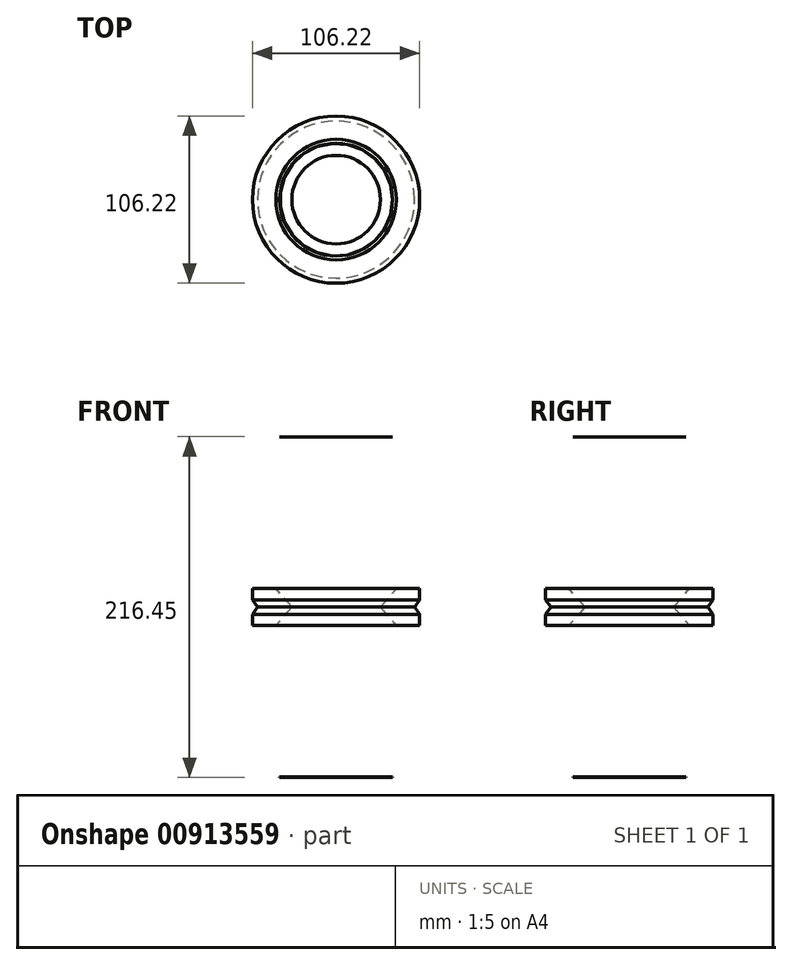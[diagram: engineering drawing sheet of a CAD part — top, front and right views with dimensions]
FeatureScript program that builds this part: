
annotation { "Feature Type Name" : "Feature", "Feature Type Description" : "" }
export const myFeature = defineFeature(function(context is Context, id is Id, definition is map)
    precondition{}
    {
        {
            var Q0;
            Q0=qCreatedBy(makeId("Front.planeOp"),FACE);
            var sketch = newSketch(context, id + "F0", { "sketchPlane" : qUnion([Q0])});
            skLineSegment(sketch, "E0", {"start": v(0, 52.95) * mm, "end": v(28.13, 52.95) * mm});
            skLineSegment(sketch, "E1", {"start": v(28.13, 52.95) * mm, "end": v(38.3, 64.67) * mm});
            skLineSegment(sketch, "E2", {"start": v(38.3, 64.67) * mm, "end": v(53.1, 64.67) * mm});
            skLineSegment(sketch, "E3", {"start": v(53.1, 64.67) * mm, "end": v(53.1, 57.58) * mm});
            skLineSegment(sketch, "E4", {"start": v(53.1, 57.58) * mm, "end": v(35.84, 32.91) * mm});
            skFitSpline(sketch, "E5", {"points": [v(35.84, 32.91) * mm, v(29.06, 26.13) * mm, v(35.84, 17.19) * mm, v(50.64, 9.48) * mm, v(57.73, -16.1) * mm, v(35.84, -55.27) * mm, v(35.84, -54.96) * mm], "startDerivative": vector(-72.5, -45.6) * mm, "endDerivative": vector(4.55, 19.23) * mm});
            skLineSegment(sketch, "E6", {"start": v(35.84, -54.96) * mm, "end": v(35.84, -61.74) * mm});
            skLineSegment(sketch, "E7", {"start": v(0, 66.83) * mm, "end": v(0, -75) * mm, "construction": true});
            skPoint(sketch, "E8.end.orphan", {"position": v(0, -67.6) * mm});
            skLineSegment(sketch, "E9", {"start": v(35.84, -61.74) * mm, "end": v(0, -61.74) * mm});
            skFitSpline(sketch, "E10.MirrorCS", {"points": [v(35.84, 73) * mm, v(29.06, 79.78) * mm, v(35.84, 88.72) * mm, v(50.64, 96.43) * mm, v(57.73, 122.02) * mm, v(35.84, 161.18) * mm, v(35.84, 160.87) * mm], "startDerivative": vector(-72.5, 45.6) * mm, "endDerivative": vector(4.55, -19.23) * mm});
            skFitSpline(sketch, "E11.MirrorCS", {"points": [v(35.84, 73) * mm, v(29.06, 79.78) * mm, v(35.84, 88.72) * mm, v(50.64, 96.43) * mm, v(57.73, 122.02) * mm, v(35.84, 161.18) * mm, v(35.84, 160.87) * mm], "startDerivative": vector(-72.5, 45.6) * mm, "endDerivative": vector(4.55, -19.23) * mm});
            skLineSegment(sketch, "E12.MirrorCS", {"start": v(35.84, 167.65) * mm, "end": v(0, 167.65) * mm});
            skLineSegment(sketch, "E13.MirrorCS", {"start": v(35.84, 160.87) * mm, "end": v(35.84, 167.65) * mm});
            skPoint(sketch, "E14.orphan", {"position": v(53.1, 41.24) * mm});
            skPoint(sketch, "E15.MirrorCS.start.orphan", {"position": v(38.3, 41.24) * mm});
            skPoint(sketch, "E16.MirrorCS.start.orphan", {"position": v(28.13, 52.95) * mm});
            skPoint(sketch, "E17.orphan", {"position": v(53.1, 48.33) * mm});
            skPoint(sketch, "E18.MirrorP", {"position": v(38.3, 64.67) * mm});
            skLineSegment(sketch, "E19.MirrorCS", {"start": v(53.1, 48.33) * mm, "end": v(35.84, 73) * mm});
            skFitSpline(sketch, "E20.MirrorCS", {"points": [v(35.84, 73) * mm, v(29.06, 79.78) * mm, v(35.84, 88.72) * mm, v(50.64, 96.43) * mm, v(57.73, 122.02) * mm, v(35.84, 161.18) * mm, v(35.84, 160.87) * mm], "startDerivative": vector(-72.5, 45.6) * mm, "endDerivative": vector(4.55, -19.23) * mm});
            skLineSegment(sketch, "E21.MirrorCS", {"start": v(28.13, 52.95) * mm, "end": v(38.3, 41.24) * mm});
            skLineSegment(sketch, "E22.MirrorCS", {"start": v(38.3, 41.24) * mm, "end": v(53.1, 41.24) * mm});
            skPoint(sketch, "E23.MirrorP", {"position": v(53.1, 64.67) * mm});
            skLineSegment(sketch, "E24.MirrorCS", {"start": v(53.1, 41.24) * mm, "end": v(53.1, 48.33) * mm});
            skPoint(sketch, "E25.MirrorP", {"position": v(53.1, 57.58) * mm});
            skSolve(sketch);
        }
        {
            var Q0;
            Q0 = qSketchRegion(id + "F0", true);
            var Q1;
            Q1=sQuery(id+"F0.wireOp",EDGE,"E0");
            var Q2;
            Q2=sQuery(id+"F0.wireOp",EDGE,"E1");
            var Q3;
            Q3=sQuery(id+"F0.wireOp",EDGE,"E2");
            var Q4;
            Q4=sQuery(id+"F0.wireOp",EDGE,"E3");
            var Q5;
            Q5=sQuery(id+"F0.wireOp",EDGE,"E4");
            var Q6;
            Q6=sQuery(id+"F0.wireOp",EDGE,"4dhwL9r9-vrLl-ybkp-hvaQ-uPYx3Jr7oyYk");
            var Q7;
            Q7=sQuery(id+"F0.wireOp",EDGE,"E8");
            var Q8;
            Q8=sQuery(id+"F0.wireOp",EDGE,"E5");
            var Q9;
            Q9=sQuery(id+"F0.wireOp",EDGE,"E7");
            revolve(context, id + "F1", {"surfaceOperationType" : NewSurfaceOperationType.NEW, "entities" : qUnion([Q0]), "surfaceEntities" : qUnion([Q1, Q2, Q3, Q4, Q5, Q6, Q7, Q8]), "axis" : qUnion([Q9]), "revolveType" : RevolveType.FULL});
        }
    });
